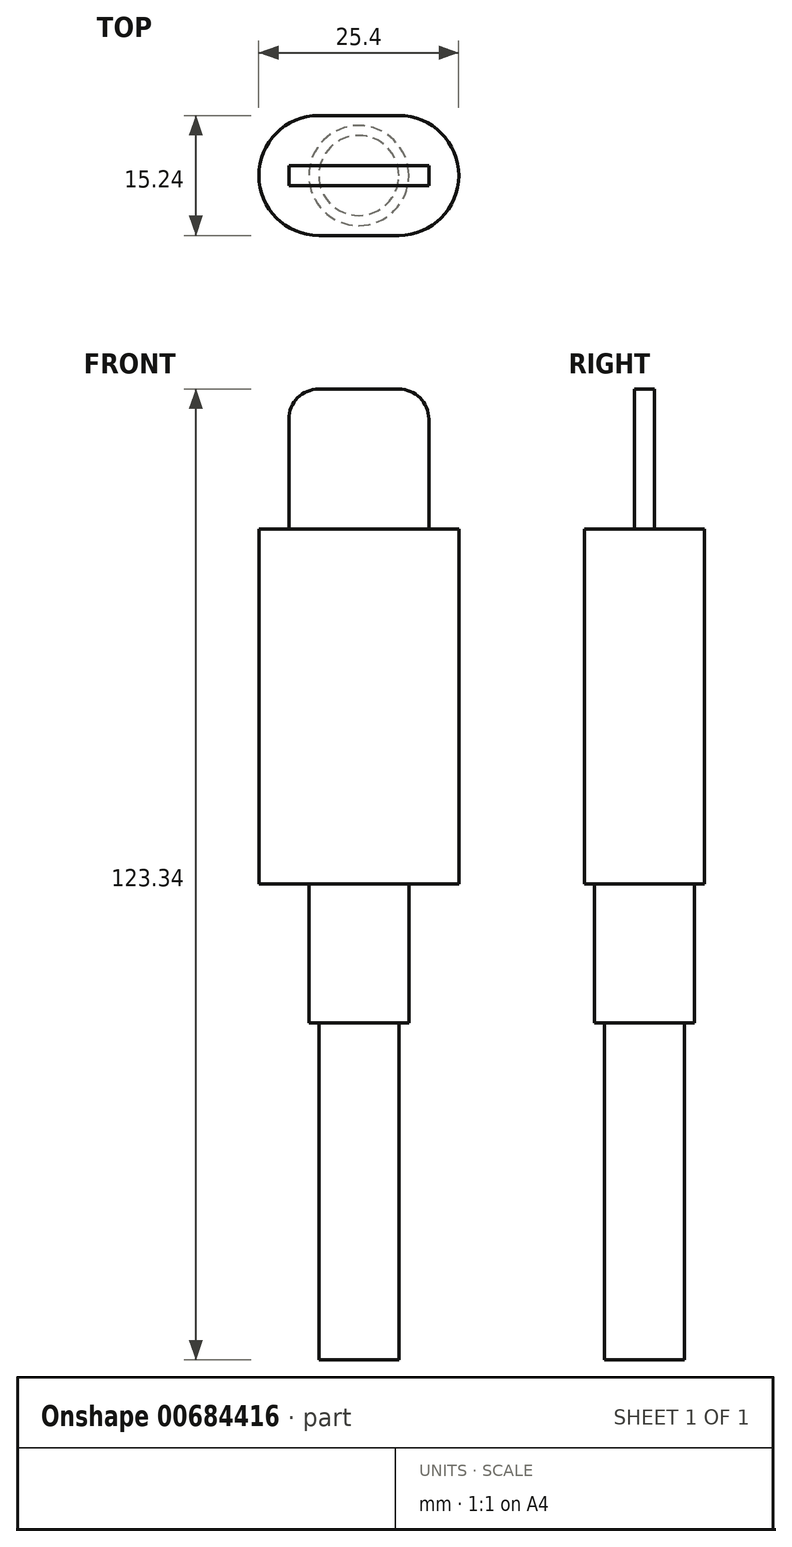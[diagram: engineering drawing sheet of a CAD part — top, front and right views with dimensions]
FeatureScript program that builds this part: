
annotation { "Feature Type Name" : "Feature", "Feature Type Description" : "" }
export const myFeature = defineFeature(function(context is Context, id is Id, definition is map)
    precondition{}
    {
        {
            var Q0;
            Q0=qCreatedBy(makeId("Front.planeOp"),FACE);
            var sketch = newSketch(context, id + "F0", { "sketchPlane" : qUnion([Q0])});
            skLineSegment(sketch, "E0.bottom", {"start": v(-39.35, 20.1) * mm, "end": v(-64.75, 20.1) * mm});
            skLineSegment(sketch, "E0.top", {"start": v(-39.35, 65.18) * mm, "end": v(-64.75, 65.18) * mm});
            skLineSegment(sketch, "E0.left", {"start": v(-39.35, 20.1) * mm, "end": v(-39.35, 65.18) * mm});
            skLineSegment(sketch, "E0.right", {"start": v(-64.75, 20.1) * mm, "end": v(-64.75, 65.18) * mm});
            skPoint(sketch, "E0.middle", {"position": v(-52.05, 42.64) * mm});
            skLineSegment(sketch, "E1", {"start": v(-58.4, 20.1) * mm, "end": v(-58.4, 2.46) * mm});
            skLineSegment(sketch, "E2", {"start": v(-58.4, 2.46) * mm, "end": v(-45.7, 2.46) * mm});
            skLineSegment(sketch, "E3", {"start": v(-45.7, 2.46) * mm, "end": v(-45.7, 20.1) * mm});
            skLineSegment(sketch, "E4", {"start": v(-57.13, 2.46) * mm, "end": v(-57.13, -40.38) * mm});
            skLineSegment(sketch, "E5", {"start": v(-57.13, -40.38) * mm, "end": v(-46.97, -40.38) * mm});
            skLineSegment(sketch, "E6", {"start": v(-46.97, -40.38) * mm, "end": v(-46.97, 2.46) * mm});
            skLineSegment(sketch, "E7", {"start": v(-60.94, 65.18) * mm, "end": v(-60.94, 79.15) * mm});
            skLineSegment(sketch, "E8", {"start": v(-57.13, 82.96) * mm, "end": v(-46.97, 82.96) * mm});
            skLineSegment(sketch, "E9", {"start": v(-43.16, 79.15) * mm, "end": v(-43.16, 65.18) * mm});
            skPoint(sketch, "E10.visualSharp", {"position": v(-60.94, 82.96) * mm});
            skArc(sketch, "E10.filletArc", {"start": v(-57.13, 82.96) * mm, "mid": v(-59.82, 81.84) * mm, "end": v(-60.94, 79.15) * mm});
            skPoint(sketch, "E11.visualSharp", {"position": v(-43.16, 82.96) * mm});
            skArc(sketch, "E11.filletArc", {"start": v(-43.16, 79.15) * mm, "mid": v(-44.27, 81.84) * mm, "end": v(-46.97, 82.96) * mm});
            skLineSegment(sketch, "E12", {"start": v(-52.05, 20.1) * mm, "end": v(-52.05, -40.38) * mm});
            skSolve(sketch);
        }
        {
            var Q0;
            {var subQ0=sQuery(id+"F0.wireOp",EDGE,"E0.left");Q0=makeQuery(id+"F0.imprint","IMPRINT",FACE,{"disambiguationData":[TD([[makeQuery(id+"F0.imprint","IMPRINT",EDGE,{"derivedFrom":subQ0}),1.0]])]});}
            extrude(context, id + "F1", {"entities" : qUnion([Q0]), "endBound" : BoundingType.SYMMETRIC, "depth" : 15.24 * mm, "offsetDistance" : 25.4 * mm});
        }
        {
            var Q0;
            {var subQ1=sQuery(id+"F0.wireOp",EDGE,"E7");Q0=makeQuery(id+"F0.imprint","IMPRINT",FACE,{"disambiguationData":[TD([[makeQuery(id+"F0.imprint","IMPRINT",EDGE,{"derivedFrom":subQ1}),-1.0]])]});}
            extrude(context, id + "F2", {"entities" : qUnion([Q0]), "operationType" : NewBodyOperationType.ADD, "endBound" : BoundingType.SYMMETRIC, "depth" : 2.54 * mm, "offsetDistance" : 25.4 * mm});
        }
        {
            var Q0;
            {var subQ4=sQuery(id+"F0.wireOp",EDGE,"E1");Q0=makeQuery(id+"F0.imprint","IMPRINT",FACE,{"disambiguationData":[TD([[makeQuery(id+"F0.imprint","IMPRINT",EDGE,{"derivedFrom":subQ4}),1.0]])]});}
            var Q1;
            Q1=sQuery(id+"F0.wireOp",EDGE,"E12");
            revolve(context, id + "F3", {"operationType" : NewBodyOperationType.ADD, "entities" : qUnion([Q0]), "axis" : qUnion([Q1]), "revolveType" : RevolveType.FULL});
        }
        {
            var Q0;
            {var subQ0=sQuery(id+"F0.wireOp",EDGE,"E4");Q0=makeQuery(id+"F0.imprint","IMPRINT",FACE,{"disambiguationData":[TD([[makeQuery(id+"F0.imprint","IMPRINT",EDGE,{"derivedFrom":subQ0}),1.0]])]});}
            var Q1;
            Q1=sQuery(id+"F0.wireOp",EDGE,"E12");
            revolve(context, id + "F4", {"operationType" : NewBodyOperationType.ADD, "entities" : qUnion([Q0]), "axis" : qUnion([Q1]), "revolveType" : RevolveType.FULL});
        }
        {
            var Q0;
            Q0=makeQuery(id+"F1.opExtrude","CAP_EDGE",EDGE,{"disambiguationData":[OSD([sQuery(id+"F0.wireOp",EDGE,"E0.left")])],"isStart":true});
            var Q1;
            Q1=makeQuery(id+"F1.opExtrude","CAP_EDGE",EDGE,{"disambiguationData":[OSD([sQuery(id+"F0.wireOp",EDGE,"E0.right")])],"isStart":true});
            var Q2;
            Q2=makeQuery(id+"F1.opExtrude","CAP_EDGE",EDGE,{"disambiguationData":[OSD([sQuery(id+"F0.wireOp",EDGE,"E0.right")])],"isStart":false});
            var Q3;
            Q3=makeQuery(id+"F1.opExtrude","CAP_EDGE",EDGE,{"disambiguationData":[OSD([sQuery(id+"F0.wireOp",EDGE,"E0.left")])],"isStart":false});
            fillet(context, id + "F5", {"entities" : qUnion([Q0, Q1, Q2, Q3]), "radius" : 7.62 * mm, "tangentPropagation" : true, "allowEdgeOverflow" : false});
        }
    });
